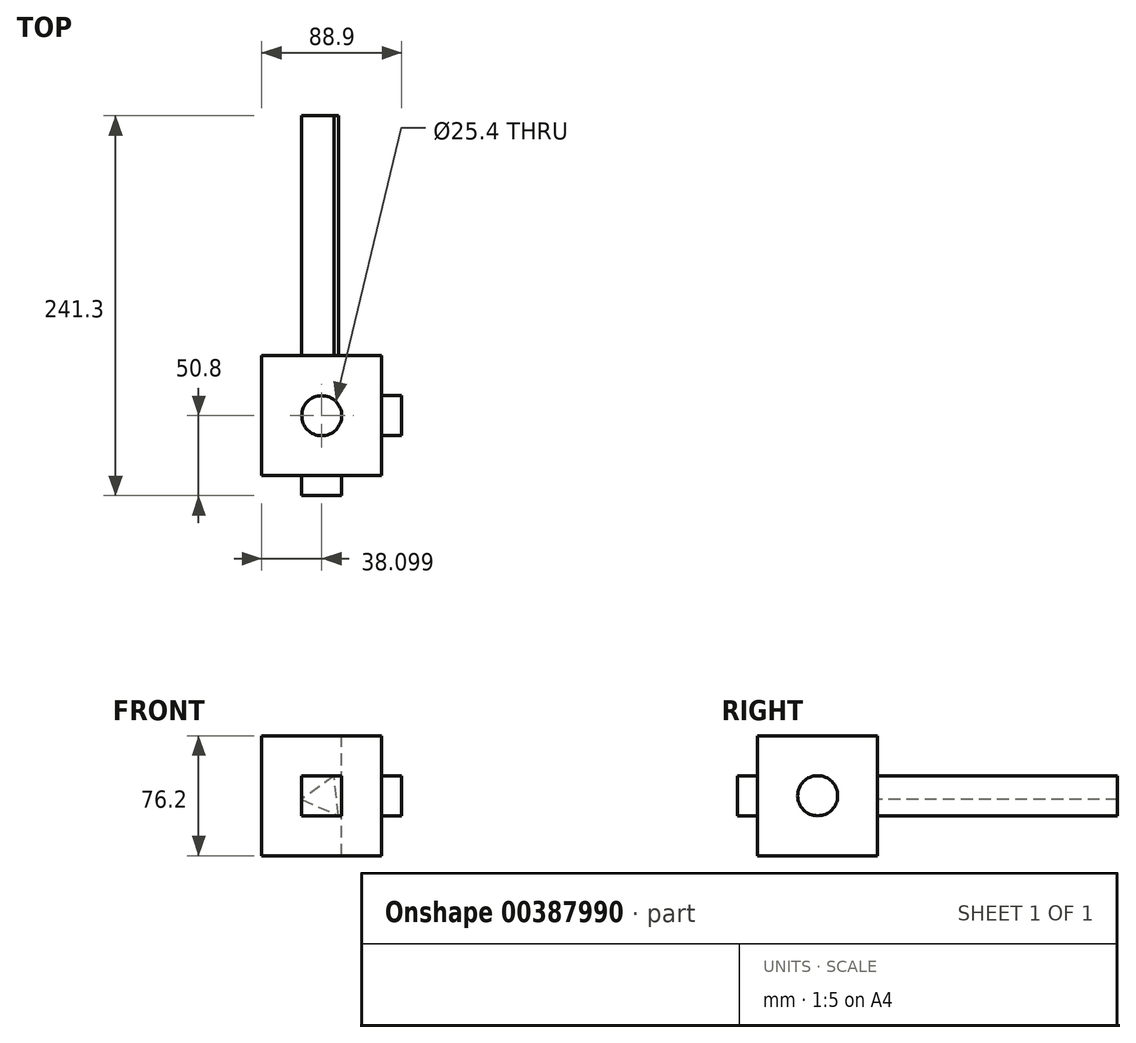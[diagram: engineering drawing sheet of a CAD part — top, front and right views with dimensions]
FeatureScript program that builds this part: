
annotation { "Feature Type Name" : "Feature", "Feature Type Description" : "" }
export const myFeature = defineFeature(function(context is Context, id is Id, definition is map)
    precondition{}
    {
        {
            var Q0;
            Q0=qCreatedBy(makeId("Front.planeOp"),FACE);
            var sketch = newSketch(context, id + "F0", { "sketchPlane" : qUnion([Q0])});
            skLineSegment(sketch, "E0.bottom", {"start": v(-56.5, 44.5) * mm, "end": v(19.7, 44.5) * mm});
            skLineSegment(sketch, "E0.top", {"start": v(-56.5, -31.7) * mm, "end": v(19.7, -31.7) * mm});
            skLineSegment(sketch, "E0.left", {"start": v(-56.5, 44.5) * mm, "end": v(-56.5, -31.7) * mm});
            skLineSegment(sketch, "E0.right", {"start": v(19.7, 44.5) * mm, "end": v(19.7, -31.7) * mm});
            skSolve(sketch);
        }
        {
            var Q0;
            Q0=makeQuery(id+"F0.imprint","IMPRINT",FACE,{"disambiguationData":[TD([[makeQuery(id+"F0.imprint","IMPRINT",EDGE,{"derivedFrom":sQuery(id+"F0.wireOp",EDGE,"E0.bottom")}),-1.0]])]});
            extrude(context, id + "F1", {"entities" : qUnion([Q0]), "depth" : 76.2 * mm});
        }
        {
            var Q0;
            Q0=makeQuery(id+"F1.opExtrude","SWEPT_FACE",FACE,{"disambiguationData":[OSD([sQuery(id+"F0.wireOp",EDGE,"E0.bottom")])]});
            var sketch = newSketch(context, id + "F2", { "sketchPlane" : qUnion([Q0])});
            skPoint(sketch, "E1", {"position": v(-18.4, -38.1) * mm});
            skSolve(sketch);
        }
        {
            var Q0;
            Q0=sQuery(id+"F2.wireOp",VERTEX,"E1");
            var Q1;
            Q1=makeQuery(id+"F1.opExtrude","SWEPT_BODY",BODY,{"disambiguationData":[OSD([sQuery(id+"F0.wireOp",EDGE,"E0.bottom"),sQuery(id+"F0.wireOp",EDGE,"E0.top"),sQuery(id+"F0.wireOp",EDGE,"E0.left"),sQuery(id+"F0.wireOp",EDGE,"E0.right")])]});
            hole(context, id + "F3", {"style" : HoleStyle.SIMPLE, "endStyle" : HoleEndStyle.THROUGH, "holeDiameter" : 25.4 * mm, "isTappedThrough" : true, "tappedDepth" : 12.7 * mm, "tapClearance" : 3, "locations" : qUnion([Q0]), "scope" : qUnion([Q1])});
        }
        {
            var Q0;
            Q0=makeQuery(id+"F1.opExtrude","CAP_FACE",FACE,{"disambiguationData":[OSD([sQuery(id+"F0.wireOp",EDGE,"E0.bottom"),sQuery(id+"F0.wireOp",EDGE,"E0.top"),sQuery(id+"F0.wireOp",EDGE,"E0.left"),sQuery(id+"F0.wireOp",EDGE,"E0.right")])],"isStart":false});
            var sketch = newSketch(context, id + "F4", { "sketchPlane" : qUnion([Q0])});
            skLineSegment(sketch, "E2.bottom", {"start": v(-31.1, 19.1) * mm, "end": v(-5.7, 19.1) * mm});
            skLineSegment(sketch, "E2.top", {"start": v(-31.1, -6.3) * mm, "end": v(-5.7, -6.3) * mm});
            skLineSegment(sketch, "E2.left", {"start": v(-31.1, 19.1) * mm, "end": v(-31.1, -6.3) * mm});
            skLineSegment(sketch, "E2.right", {"start": v(-5.7, 19.1) * mm, "end": v(-5.7, -6.3) * mm});
            skSolve(sketch);
        }
        {
            var Q0;
            Q0=makeQuery(id+"F4.imprint","IMPRINT",FACE,{"disambiguationData":[TD([[makeQuery(id+"F4.imprint","IMPRINT",EDGE,{"derivedFrom":sQuery(id+"F4.wireOp",EDGE,"E2.bottom")}),-1.0]])]});
            extrude(context, id + "F5", {"entities" : qUnion([Q0]), "operationType" : NewBodyOperationType.ADD, "depth" : 12.7 * mm});
        }
        {
            var Q0;
            Q0=makeQuery(id+"F1.opExtrude","SWEPT_FACE",FACE,{"disambiguationData":[OSD([sQuery(id+"F0.wireOp",EDGE,"E0.right")])]});
            var sketch = newSketch(context, id + "F6", { "sketchPlane" : qUnion([Q0])});
            skCircle(sketch, "E3", {"center": v(-38.1, 6.4) * mm, "radius": 12.7 * mm});
            skSolve(sketch);
        }
        {
            var Q0;
            Q0 = qSketchRegion(id + "F6", true);
            extrude(context, id + "F7", {"entities" : qUnion([Q0]), "operationType" : NewBodyOperationType.ADD, "depth" : 12.7 * mm});
        }
        {
            var Q0;
            Q0=makeQuery(id+"F1.opExtrude","CAP_FACE",FACE,{"disambiguationData":[OSD([sQuery(id+"F0.wireOp",EDGE,"E0.bottom"),sQuery(id+"F0.wireOp",EDGE,"E0.top"),sQuery(id+"F0.wireOp",EDGE,"E0.left"),sQuery(id+"F0.wireOp",EDGE,"E0.right")])],"isStart":true});
            var sketch = newSketch(context, id + "F8", { "sketchPlane" : qUnion([Q0])});
            skCircle(sketch, "E4.cCircle", {"center": v(16.54, 5.6) * mm, "radius": 7.38 * mm, "construction": true});
            skLineSegment(sketch, "E4.0", {"start": v(31.2, 4.01) * mm, "end": v(7.83, -6.3) * mm});
            skLineSegment(sketch, "E4.1", {"start": v(7.83, -6.3) * mm, "end": v(10.58, 19.1) * mm});
            skLineSegment(sketch, "E4.2", {"start": v(10.58, 19.1) * mm, "end": v(31.2, 4.01) * mm});
            skPoint(sketch, "E4.0.midPoint", {"position": v(19.52, -1.15) * mm});
            skSolve(sketch);
        }
        {
            var Q0;
            Q0 = qSketchRegion(id + "F8", true);
            extrude(context, id + "F9", {"entities" : qUnion([Q0]), "operationType" : NewBodyOperationType.ADD, "depth" : 152.4 * mm});
        }
    });
